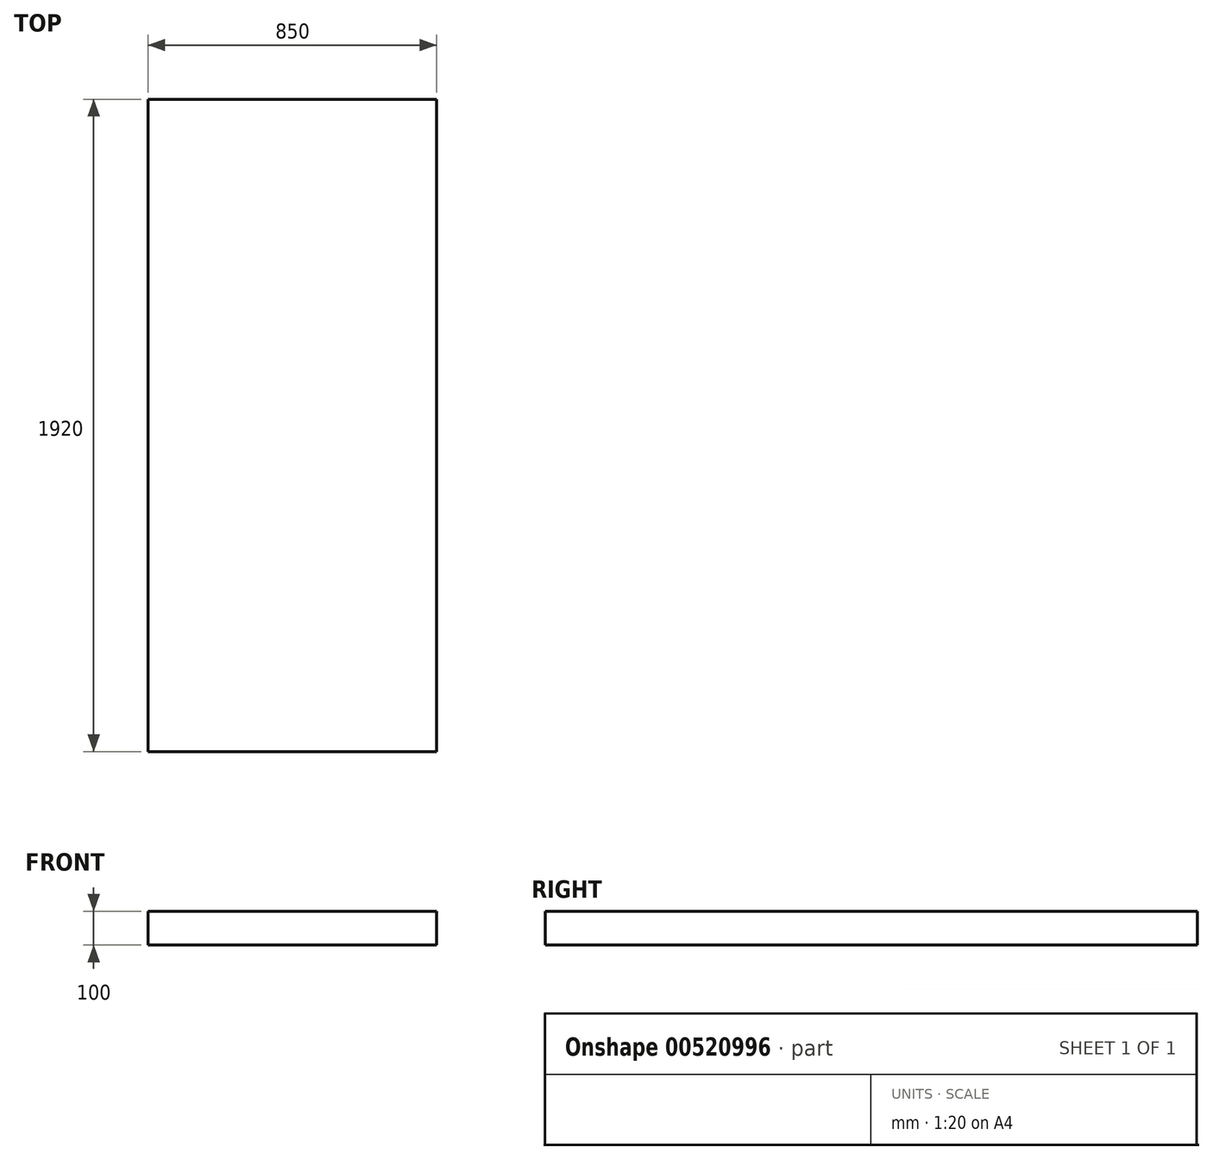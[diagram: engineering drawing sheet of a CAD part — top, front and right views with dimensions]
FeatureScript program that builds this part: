
annotation { "Feature Type Name" : "Feature", "Feature Type Description" : "" }
export const myFeature = defineFeature(function(context is Context, id is Id, definition is map)
    precondition{}
    {
        {
            var Q0;
            Q0=qCreatedBy(makeId("Top.planeOp"),FACE);
            var sketch = newSketch(context, id + "F0", { "sketchPlane" : qUnion([Q0])});
            skLineSegment(sketch, "E0.bottom", {"start": v(-425, 960) * mm, "end": v(425, 960) * mm});
            skLineSegment(sketch, "E0.top", {"start": v(-425, -960) * mm, "end": v(425, -960) * mm});
            skLineSegment(sketch, "E0.left", {"start": v(-425, 960) * mm, "end": v(-425, -960) * mm});
            skLineSegment(sketch, "E0.right", {"start": v(425, 960) * mm, "end": v(425, -960) * mm});
            skPoint(sketch, "E0.middle", {"position": v(0, 0) * mm});
            skSolve(sketch);
        }
        {
            var Q0;
            Q0 = qSketchRegion(id + "F0", true);
            extrude(context, id + "F1", {"entities" : qUnion([Q0]), "depth" : 100 * mm, "offsetDistance" : 25 * mm});
        }
    });
